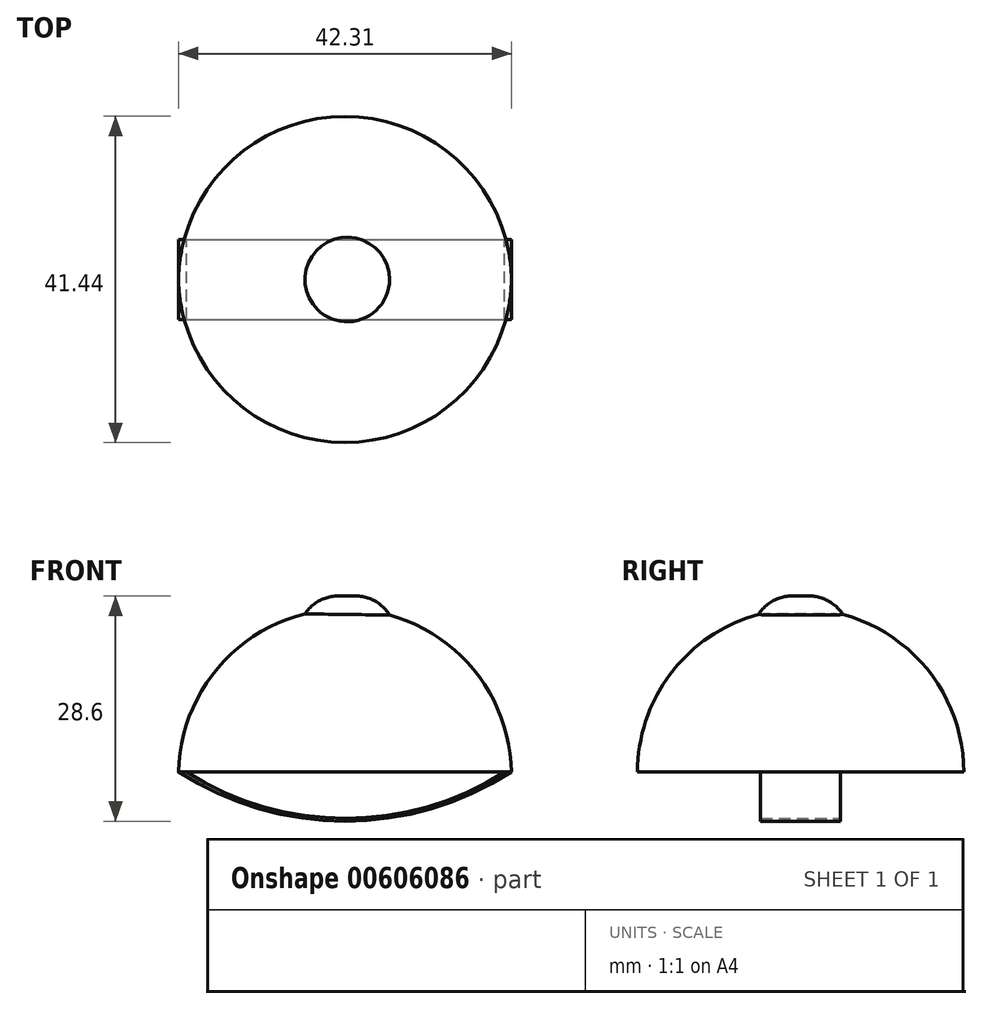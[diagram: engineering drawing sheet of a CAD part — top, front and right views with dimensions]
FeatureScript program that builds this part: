
annotation { "Feature Type Name" : "Feature", "Feature Type Description" : "" }
export const myFeature = defineFeature(function(context is Context, id is Id, definition is map)
    precondition{}
    {
        {
            var Q0;
            Q0=qCreatedBy(makeId("Front.planeOp"),FACE);
            var sketch = newSketch(context, id + "F0", { "sketchPlane" : qUnion([Q0])});
            skLineSegment(sketch, "E0", {"start": v(-21.44, 0) * mm, "end": v(20.87, 0) * mm});
            skArc(sketch, "E1", {"start": v(20.87, 0) * mm, "mid": v(-0.29, 20.72) * mm, "end": v(-21.44, 0) * mm});
            skSolve(sketch);
        }
        {
            var Q0;
            Q0 = qSketchRegion(id + "F0", true);
            var Q1;
            Q1=sQuery(id+"F0.wireOp",EDGE,"E0");
            revolve(context, id + "F1", {"entities" : qUnion([Q0]), "axis" : qUnion([Q1]), "revolveType" : RevolveType.TWO_DIRECTIONS, "angle" : 90 * degree, "angleBack" : 270 * degree});
        }
        {
            var Q0;
            Q0=qCreatedBy(makeId("Front.planeOp"),FACE);
            var sketch = newSketch(context, id + "F2", { "sketchPlane" : qUnion([Q0])});
            skArc(sketch, "E2", {"start": v(-21.4, 0) * mm, "mid": v(-0.28, -6.25) * mm, "end": v(20.86, 0) * mm});
            skArc(sketch, "E3", {"start": v(-20.4, 0) * mm, "mid": v(-0.22, -5.9) * mm, "end": v(19.96, 0) * mm});
            skLineSegment(sketch, "E4", {"start": v(19.96, 0) * mm, "end": v(20.86, 0) * mm});
            skLineSegment(sketch, "E5", {"start": v(-20.4, 0) * mm, "end": v(-21.4, 0) * mm});
            skSolve(sketch);
        }
        {
            var Q0;
            Q0 = qSketchRegion(id + "F2", true);
            extrude(context, id + "F3", {"entities" : qUnion([Q0]), "operationType" : NewBodyOperationType.ADD, "depth" : 5.08 * mm, "offsetDistance" : 25.4 * mm, "hasSecondDirection" : true, "secondDirectionOppositeDirection" : true, "secondDirectionDepth" : 5.08 * mm});
        }
        {
            var Q0;
            Q0=qCreatedBy(makeId("Top.planeOp"),FACE);
            var sketch = newSketch(context, id + "F4", { "sketchPlane" : qUnion([Q0])});
            skCircle(sketch, "E6", {"center": v(0, 0) * mm, "radius": 5.37 * mm});
            skSolve(sketch);
        }
        {
            var Q0;
            Q0 = qSketchRegion(id + "F4", true);
            extrude(context, id + "F5", {"entities" : qUnion([Q0]), "operationType" : NewBodyOperationType.ADD, "depth" : 22.35 * mm, "offsetDistance" : 25.4 * mm});
        }
        {
            var Q0;
            Q0=makeQuery(id+"F5.opExtrude","CAP_EDGE",EDGE,{"disambiguationData":[OSD([sQuery(id+"F4.wireOp",EDGE,"E6")])],"isStart":false});
            fillet(context, id + "F6", {"entities" : qUnion([Q0]), "radius" : 5.08 * mm, "tangentPropagation" : true, "allowEdgeOverflow" : false});
        }
    });
